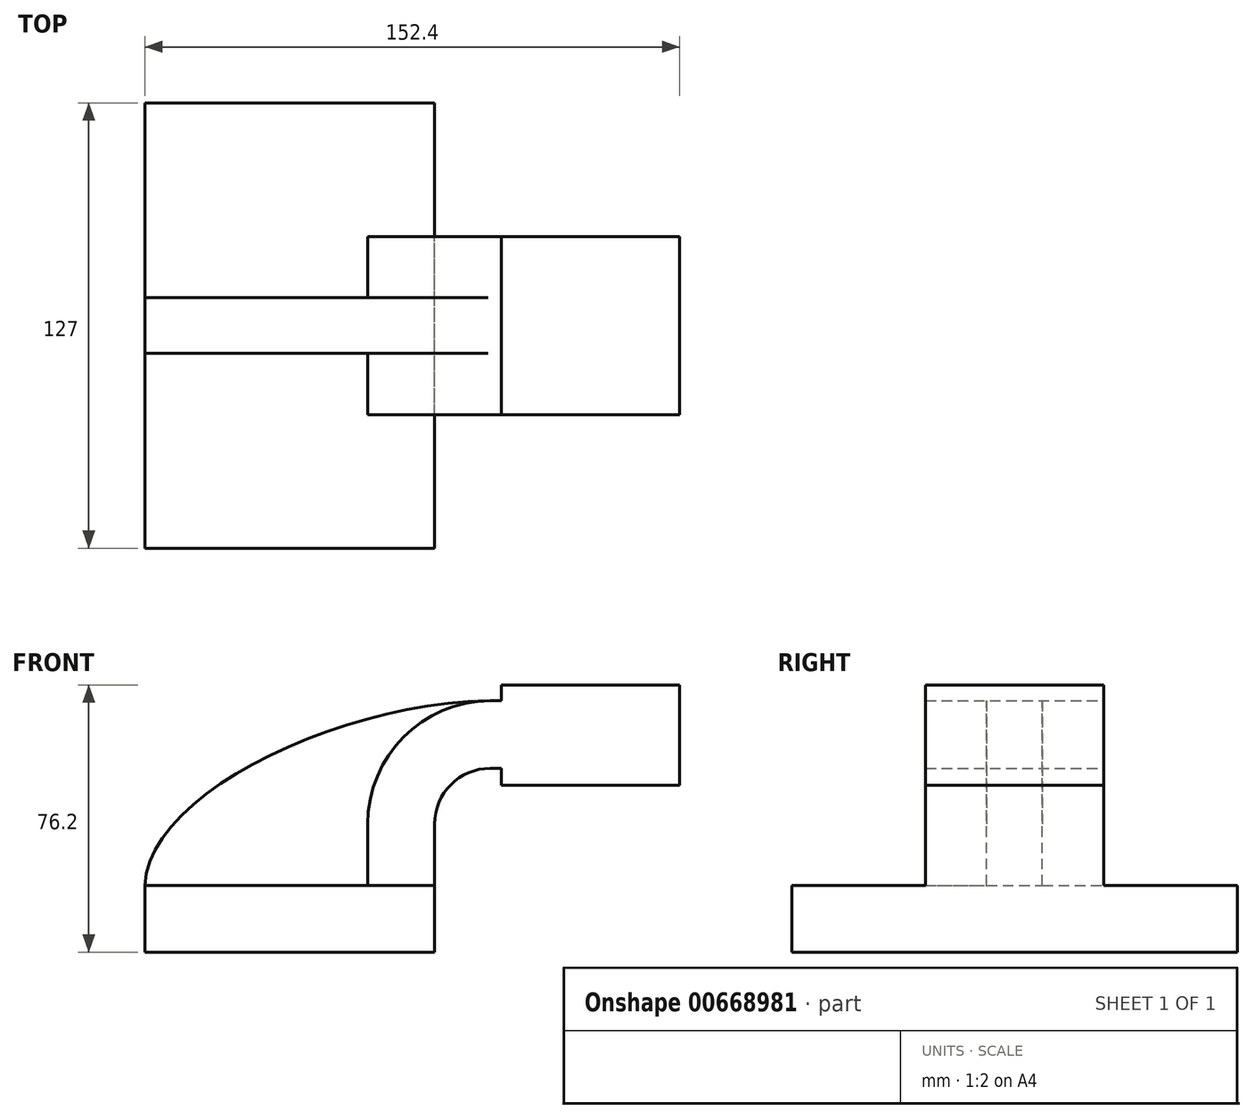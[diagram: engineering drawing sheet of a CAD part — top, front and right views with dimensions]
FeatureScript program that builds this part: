
annotation { "Feature Type Name" : "Feature", "Feature Type Description" : "" }
export const myFeature = defineFeature(function(context is Context, id is Id, definition is map)
    precondition{}
    {
        {
            var Q0;
            Q0=qCreatedBy(makeId("Front.planeOp"),FACE);
            var sketch = newSketch(context, id + "F0", { "sketchPlane" : qUnion([Q0])});
            skLineSegment(sketch, "E0.bottom", {"start": v(-41.28, 9.53) * mm, "end": v(41.28, 9.53) * mm});
            skLineSegment(sketch, "E0.top", {"start": v(-41.28, -9.53) * mm, "end": v(41.28, -9.53) * mm});
            skLineSegment(sketch, "E0.left", {"start": v(-41.28, 9.53) * mm, "end": v(-41.28, -9.53) * mm});
            skLineSegment(sketch, "E0.right", {"start": v(41.28, 9.53) * mm, "end": v(41.28, -9.53) * mm});
            skPoint(sketch, "E0.middle", {"position": v(0, 0) * mm});
            skLineSegment(sketch, "E1.bottom", {"start": v(111.12, 66.67) * mm, "end": v(60.33, 66.67) * mm});
            skLineSegment(sketch, "E1.top", {"start": v(111.12, 38.1) * mm, "end": v(60.33, 38.1) * mm});
            skLineSegment(sketch, "E1.left", {"start": v(111.12, 66.68) * mm, "end": v(111.12, 38.1) * mm});
            skLineSegment(sketch, "E1.right", {"start": v(60.32, 66.68) * mm, "end": v(60.33, 38.1) * mm});
            skPoint(sketch, "E1.middle", {"position": v(85.72, 52.39) * mm});
            skLineSegment(sketch, "E2", {"start": v(41.27, 9.53) * mm, "end": v(41.27, 27) * mm});
            skArc(sketch, "E3", {"start": v(41.28, 27) * mm, "mid": v(45.92, 38.23) * mm, "end": v(57.15, 42.88) * mm});
            skLineSegment(sketch, "E4", {"start": v(57.15, 42.88) * mm, "end": v(89.2, 42.88) * mm});
            skLineSegment(sketch, "E5.0", {"start": v(22.23, 9.53) * mm, "end": v(22.23, 27) * mm});
            skLineSegment(sketch, "E6.0", {"start": v(57.15, 62.18) * mm, "end": v(89.2, 62.18) * mm});
            skFitSpline(sketch, "E7", {"points": [v(-41.28, 9.53) * mm, v(57.15, 62.18) * mm], "startDerivative": vector(2.83, 78.78) * mm, "endDerivative": vector(128.66, 1.8) * mm});
            skArc(sketch, "E8", {"start": v(22.23, 27) * mm, "mid": v(32.44, 51.79) * mm, "end": v(57.15, 62.18) * mm});
            skSolve(sketch);
        }
        {
            var Q0;
            Q0=makeQuery(id+"F0.imprint","IMPRINT",FACE,{"disambiguationData":[TD([[makeQuery(id+"F0.imprint","IMPRINT",EDGE,{"derivedFrom":sQuery(id+"F0.wireOp",EDGE,"E0.top")}),1.0]])]});
            extrude(context, id + "F1", {"entities" : qUnion([Q0]), "endBound" : BoundingType.SYMMETRIC, "depth" : 127 * mm, "offsetDistance" : 25.4 * mm});
        }
        {
            var Q0;
            {var subQ1=sQuery(id+"F0.wireOp",EDGE,"E1.bottom");Q0=makeQuery(id+"F0.imprint","IMPRINT",FACE,{"disambiguationData":[TD([[makeQuery(id+"F0.imprint","IMPRINT",EDGE,{"derivedFrom":subQ1}),1.0]])]});}
            var Q1;
            {var subQ0=sQuery(id+"F0.wireOp",EDGE,"E8");var subQ1=sQuery(id+"F0.wireOp",EDGE,"E7");var subQ3=makeQuery(id+"F0.imprint","INTERSECT",VERTEX,{"derivedFrom":[subQ1,subQ0]});Q1=makeQuery(id+"F0.imprint","IMPRINT",FACE,{"disambiguationData":[TD([[makeQuery(id+"F0.imprint","IMPRINT",EDGE,{"disambiguationData":[TD([[subQ3,-1.0]])],"derivedFrom":subQ1}),1.0]])]});}
            var Q2;
            Q2=makeQuery(id+"F0.imprint","IMPRINT",FACE,{"disambiguationData":[TD([[makeQuery(id+"F0.imprint","IMPRINT",EDGE,{"derivedFrom":sQuery(id+"F0.wireOp",EDGE,"E0.top")}),1.0]])]});
            var Q3;
            {var subQ1=sQuery(id+"F0.wireOp",EDGE,"E2");Q3=makeQuery(id+"F0.imprint","IMPRINT",FACE,{"disambiguationData":[TD([[makeQuery(id+"F0.imprint","IMPRINT",EDGE,{"derivedFrom":subQ1}),1.0]])]});}
            extrude(context, id + "F2", {"entities" : qUnion([Q0, Q1, Q2, Q3]), "operationType" : NewBodyOperationType.ADD, "endBound" : BoundingType.SYMMETRIC, "depth" : 50.8 * mm, "offsetDistance" : 25.4 * mm});
        }
        {
            var Q0;
            {var subQ3=sQuery(id+"F0.wireOp",EDGE,"E5.0");Q0=makeQuery(id+"F0.imprint","IMPRINT",FACE,{"disambiguationData":[TD([[makeQuery(id+"F0.imprint","IMPRINT",EDGE,{"derivedFrom":subQ3}),1.0]])]});}
            extrude(context, id + "F3", {"entities" : qUnion([Q0]), "operationType" : NewBodyOperationType.ADD, "endBound" : BoundingType.SYMMETRIC, "depth" : 15.88 * mm, "offsetDistance" : 25.4 * mm});
        }
    });
